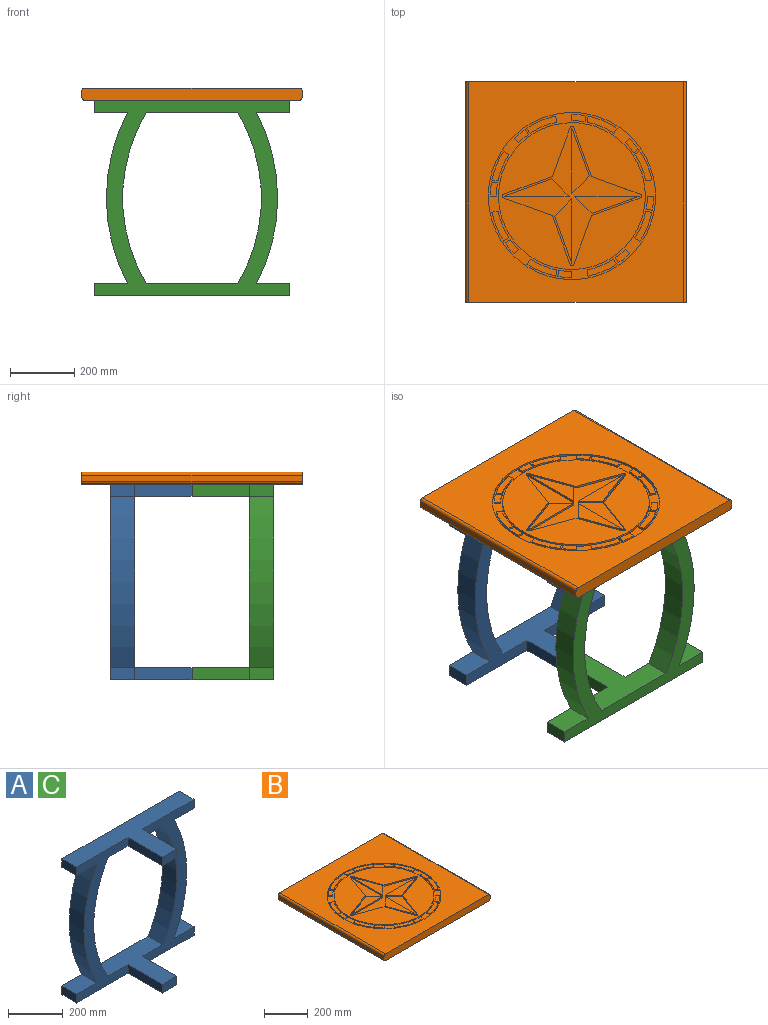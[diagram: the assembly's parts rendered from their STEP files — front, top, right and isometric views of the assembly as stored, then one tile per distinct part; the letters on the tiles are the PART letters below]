
ASSEMBLY  parts=3 mates=2
PART A: 25 faces, bbox 609.6x254x609.6 mm
  f0: plane 609.6x266.7mm, normal (0,-1,0), area 48635.2mm2, adj f2,f3,f4,f5,f6,f7,f8,f13
  f1: plane 609.6x266.7mm, normal (0,-1,0), area 48635.2mm2, adj f2,f8,f9,f10,f11,f12,f14,f15
  f2: plane 609.6x254mm, normal (0,0,1), area 59999.9mm2, adj f0,f1,f3,f17,f18,f22,f23,f24
  f3: plane 76.2x38.1mm, normal (-1,0,0), area 2903.2mm2, adj f0,f2,f4,f18
  f4: plane 104.15x76.2mm, normal (0,0,-1), area 7936mm2, adj f0,f3,f5,f18
  f5: cylinder r=571.5mm len=533.4mm, axis (0,1,0), area 42287mm2, adj f0,f4,f6,f18
  f6: plane 104.15x76.2mm, normal (0,0,1), area 7936mm2, adj f0,f5,f7,f18
  f7: plane 76.2x38.1mm, normal (-1,0,0), area 2903.2mm2, adj f0,f6,f8,f18
  f8: plane 609.6x254mm, normal (0,0,-1), area 59999.9mm2, adj f0,f1,f7,f9,f18,f19,f20,f21
  f9: plane 76.2x38.1mm, normal (1,0,0), area 2903.2mm2, adj f1,f8,f10,f18
  f10: plane 104.15x76.2mm, normal (0,0,1), area 7936mm2, adj f1,f9,f11,f18
  f11: cylinder r=571.5mm len=533.4mm, axis (0,1,0), area 42287mm2, adj f1,f10,f12,f18
  f12: plane 104.15x76.2mm, normal (0,0,-1), area 7936mm2, adj f1,f11,f17,f18
  f13: cylinder r=520.7mm len=533.4mm, axis (0,1,0), area 42672.1mm2, adj f0,f14,f16,f18
  f14: plane 284.83x254mm, normal (0,0,-1), area 35252.1mm2, adj f0,f1,f13,f15,f18,f22,f23,f24
  f15: cylinder r=520.7mm len=533.4mm, axis (0,1,0), area 42672.1mm2, adj f1,f14,f16,f18
  f16: plane 284.83x254mm, normal (0,0,1), area 35252.1mm2, adj f0,f1,f13,f15,f18,f19,f20,f21
  f17: plane 76.2x38.1mm, normal (1,0,0), area 2903.2mm2, adj f1,f2,f12,f18
  f18: plane 609.6x609.6mm, normal (0,1,0), area 103076.8mm2, adj f2,f3,f4,f5,f6,f7,f8,f9
  f19: plane 177.8x38.1mm, normal (-1,0,0), area 6774.2mm2, adj f0,f8,f16,f21
  f20: plane 177.8x38.1mm, normal (1,0,0), area 6774.2mm2, adj f1,f8,f16,f21
  f21: plane 76.2x38.1mm, normal (0,-1,0), area 2903.2mm2, adj f8,f16,f19,f20
  f22: plane 177.8x38.1mm, normal (-1,0,0), area 6774.2mm2, adj f0,f2,f14,f24
  f23: plane 177.8x38.1mm, normal (1,0,0), area 6774.2mm2, adj f1,f2,f14,f24
  f24: plane 76.2x38.1mm, normal (0,-1,0), area 2903.2mm2, adj f2,f14,f22,f23
PART B: 123 faces, bbox 685.8x685.8x38.1 mm
  f0: plane 457.2x457.2mm, normal (0,0,1), area 108640mm2, adj f76,f96,f97,f98,f99,f100,f101,f102
  f1: plane 685.8x666.75mm, normal (0,0,1), area 244313.3mm2, adj f3,f5,f9,f10,f59
  f2: plane 685.8x19.05mm, normal (-1,0,0), area 13064.5mm2, adj f3,f5,f8,f10
  f3: plane 685.8x38.1mm, normal (0,-1,0), area 26051.1mm2, adj f1,f2,f4,f6,f7,f8,f9,f10
  f4: plane 685.8x19.05mm, normal (1,0,0), area 13064.5mm2, adj f3,f5,f7,f9
  f5: plane 685.8x38.1mm, normal (0,1,0), area 26051.1mm2, adj f1,f2,f4,f6,f7,f8,f9,f10
  f6: plane 685.8x666.75mm, normal (0,0,-1), area 457257.1mm2, adj f3,f5,f7,f8
  f7: cylinder r=9.53mm len=685.8mm, axis (0,1,0), area 10260.8mm2, adj f3,f4,f5,f6
  f8: cylinder r=9.53mm len=685.8mm, axis (0,-1,0), area 10260.8mm2, adj f2,f3,f5,f6
  f9: cylinder r=9.53mm len=685.8mm, axis (0,-1,0), area 10260.8mm2, adj f1,f3,f4,f5
  f10: cylinder r=9.53mm len=685.8mm, axis (0,1,0), area 10260.8mm2, adj f1,f2,f3,f5
  f11: cylinder r=254mm len=90.1mm, axis (0,0,1), area 623.1mm2, adj f12,f60,f77,f93
  f12: plane 18.77x6.35mm, normal (0.17,-0.98,0), area 121mm2, adj f11,f13,f77,f93
  f13: cylinder r=234.95mm len=82.47mm, axis (0,0,1), area 570.3mm2, adj f12,f60,f77,f93
  f14: cylinder r=254mm len=33.92mm, axis (0,0,1), area 281.5mm2, adj f15,f61,f77,f92
  f15: plane 15.61x10.93mm, normal (0.57,-0.82,0), area 121mm2, adj f14,f16,f77,f92
  f16: cylinder r=234.95mm len=31.37mm, axis (0,0,1), area 260.4mm2, adj f15,f61,f77,f92
  f17: cylinder r=254mm len=33.92mm, axis (0,0,1), area 281.5mm2, adj f18,f62,f77,f91
  f18: plane 15.61x10.93mm, normal (0.82,0.57,0), area 121mm2, adj f17,f19,f77,f91
  f19: cylinder r=234.95mm len=31.37mm, axis (0,0,1), area 260.4mm2, adj f18,f62,f77,f91
  f20: cylinder r=254mm len=90.1mm, axis (0,0,1), area 623.1mm2, adj f21,f63,f77,f90
  f21: plane 15.61x10.93mm, normal (0.57,0.82,0), area 121mm2, adj f20,f22,f77,f90
  f22: cylinder r=234.95mm len=82.47mm, axis (0,0,1), area 570.3mm2, adj f21,f63,f77,f90
  f23: cylinder r=254mm len=44.11mm, axis (0,0,1), area 281.5mm2, adj f24,f64,f77,f89
  f24: plane 18.76x6.35mm, normal (0.17,0.98,0), area 121mm2, adj f23,f25,f77,f89
  f25: cylinder r=234.95mm len=40.8mm, axis (0,0,1), area 260.4mm2, adj f24,f64,f77,f89
  f26: cylinder r=254mm len=90.1mm, axis (0,0,1), area 623.1mm2, adj f27,f65,f77,f88
  f27: plane 18.77x6.35mm, normal (-0.17,0.98,0), area 121mm2, adj f26,f28,f77,f88
  f28: cylinder r=234.95mm len=82.47mm, axis (0,0,1), area 570.3mm2, adj f27,f65,f77,f88
  f29: cylinder r=254mm len=33.92mm, axis (0,0,1), area 281.5mm2, adj f30,f66,f77,f87
  f30: plane 15.61x10.93mm, normal (-0.57,0.82,0), area 121mm2, adj f29,f31,f77,f87
  f31: cylinder r=234.95mm len=31.37mm, axis (0,0,1), area 260.4mm2, adj f30,f66,f77,f87
  f32: cylinder r=254mm len=90.1mm, axis (0,0,1), area 623.1mm2, adj f33,f67,f77,f86
  f33: plane 15.61x10.93mm, normal (-0.82,0.57,0), area 121mm2, adj f32,f34,f77,f86
  f34: cylinder r=234.95mm len=82.47mm, axis (0,0,1), area 570.3mm2, adj f33,f67,f77,f86
  f35: cylinder r=254mm len=44.11mm, axis (0,0,1), area 281.5mm2, adj f36,f68,f77,f85
  f36: plane 18.76x6.35mm, normal (-0.98,0.17,0), area 121mm2, adj f35,f37,f77,f85
  f37: cylinder r=234.95mm len=40.8mm, axis (0,0,1), area 260.4mm2, adj f36,f68,f77,f85
  f38: cylinder r=254mm len=90.1mm, axis (0,0,1), area 623.1mm2, adj f39,f69,f77,f84
  f39: plane 18.77x6.35mm, normal (-0.98,-0.17,0), area 121mm2, adj f38,f40,f77,f84
  f40: cylinder r=234.95mm len=82.47mm, axis (0,0,1), area 570.3mm2, adj f39,f69,f77,f84
  f41: cylinder r=254mm len=33.92mm, axis (0,0,1), area 281.5mm2, adj f42,f70,f77,f83
  f42: plane 15.61x10.93mm, normal (-0.82,-0.57,0), area 121mm2, adj f41,f43,f77,f83
  f43: cylinder r=234.95mm len=31.37mm, axis (0,0,1), area 260.4mm2, adj f42,f70,f77,f83
  f44: cylinder r=254mm len=90.1mm, axis (0,0,1), area 623.1mm2, adj f45,f71,f77,f82
  f45: plane 15.61x10.93mm, normal (-0.57,-0.82,0), area 121mm2, adj f44,f46,f77,f82
  f46: cylinder r=234.95mm len=82.47mm, axis (0,0,1), area 570.3mm2, adj f45,f71,f77,f82
  f47: cylinder r=254mm len=44.11mm, axis (0,0,1), area 281.5mm2, adj f48,f72,f77,f81
  f48: plane 18.76x6.35mm, normal (-0.17,-0.98,0), area 121mm2, adj f47,f49,f77,f81
  f49: cylinder r=234.95mm len=40.8mm, axis (0,0,1), area 260.4mm2, adj f48,f72,f77,f81
  f50: cylinder r=234.95mm len=82.47mm, axis (0,0,1), area 570.3mm2, adj f51,f73,f77,f80
  f51: plane 18.77x6.35mm, normal (-0.98,0.17,0), area 121mm2, adj f50,f52,f77,f80
  f52: cylinder r=254mm len=90.1mm, axis (0,0,1), area 623.1mm2, adj f51,f73,f77,f80
  f53: plane 18.77x6.35mm, normal (0.98,0.17,0), area 121mm2, adj f54,f74,f77,f79
  f54: cylinder r=234.95mm len=82.47mm, axis (0,0,1), area 570.3mm2, adj f53,f55,f77,f79
  f55: plane 15.61x10.93mm, normal (-0.82,-0.57,0), area 121mm2, adj f54,f74,f77,f79
  f56: cylinder r=234.95mm len=40.8mm, axis (0,0,1), area 260.4mm2, adj f57,f75,f77,f78
  f57: plane 19.05x6.35mm, normal (-1,0,0), area 121mm2, adj f56,f58,f77,f78
  f58: cylinder r=254mm len=44.11mm, axis (0,0,1), area 281.5mm2, adj f57,f75,f77,f78
  f59: cylinder r=260.35mm len=520.7mm, axis (0,0,1), area 10387.5mm2, adj f1,f77
  f60: plane 15.61x10.93mm, normal (-0.57,0.82,0), area 121mm2, adj f11,f13,f77,f93
  f61: plane 13.47x13.47mm, normal (-0.71,0.71,0), area 121mm2, adj f14,f16,f77,f92
  f62: plane 13.47x13.47mm, normal (-0.71,-0.71,0), area 121mm2, adj f17,f19,f77,f91
  f63: plane 18.77x6.35mm, normal (-0.17,-0.98,0), area 121mm2, adj f20,f22,f77,f90
  f64: plane 19.05x6.35mm, normal (0,-1,0), area 121mm2, adj f23,f25,f77,f89
  f65: plane 15.61x10.93mm, normal (0.57,-0.82,0), area 121mm2, adj f26,f28,f77,f88
  f66: plane 13.47x13.47mm, normal (0.71,-0.71,0), area 121mm2, adj f29,f31,f77,f87
  f67: plane 18.77x6.35mm, normal (0.98,-0.17,0), area 121mm2, adj f32,f34,f77,f86
  f68: plane 19.05x6.35mm, normal (1,0,0), area 121mm2, adj f35,f37,f77,f85
  f69: plane 15.61x10.93mm, normal (0.82,0.57,0), area 121mm2, adj f38,f40,f77,f84
  f70: plane 13.47x13.47mm, normal (0.71,0.71,0), area 121mm2, adj f41,f43,f77,f83
  f71: plane 18.77x6.35mm, normal (0.17,0.98,0), area 121mm2, adj f44,f46,f77,f82
  f72: plane 19.05x6.35mm, normal (0,1,0), area 121mm2, adj f47,f49,f77,f81
  f73: plane 15.61x10.93mm, normal (0.82,-0.57,0), area 121mm2, adj f50,f52,f77,f80
  f74: cylinder r=254mm len=90.1mm, axis (0,0,1), area 623.1mm2, adj f53,f55,f77,f79
  f75: plane 18.76x6.35mm, normal (0.98,-0.17,0), area 121mm2, adj f56,f58,f77,f78
  f76: cylinder r=228.6mm len=457.2mm, axis (0,0,1), area 9120.7mm2, adj f0,f77
  f77: plane 520.7x520.7mm, normal (0,0,1), area 27946.7mm2, adj f11,f12,f13,f14,f15,f16,f17,f18
  f78: plane 44.11x22.62mm, normal (0,0,1), area 812.8mm2, adj f56,f57,f58,f75
  f79: plane 93.4x52.93mm, normal (0,0,1), area 1790.1mm2, adj f53,f54,f55,f74
  f80: plane 93.4x52.93mm, normal (0,0,1), area 1790.1mm2, adj f50,f51,f52,f73
  f81: plane 44.11x22.62mm, normal (0,0,1), area 812.8mm2, adj f47,f48,f49,f72
  f82: plane 93.4x52.93mm, normal (0,0,1), area 1790.1mm2, adj f44,f45,f46,f71
  f83: plane 44.84x41.93mm, normal (0,0,1), area 812.8mm2, adj f41,f42,f43,f70
  f84: plane 93.4x52.93mm, normal (0,0,1), area 1790.1mm2, adj f38,f39,f40,f69
  f85: plane 44.11x22.62mm, normal (0,0,1), area 812.8mm2, adj f35,f36,f37,f68
  f86: plane 93.4x52.93mm, normal (0,0,1), area 1790.1mm2, adj f32,f33,f34,f67
  f87: plane 44.84x41.93mm, normal (0,0,1), area 812.8mm2, adj f29,f30,f31,f66
  f88: plane 93.4x52.93mm, normal (0,0,1), area 1790.1mm2, adj f26,f27,f28,f65
  f89: plane 44.11x22.62mm, normal (0,0,1), area 812.8mm2, adj f23,f24,f25,f64
  f90: plane 93.4x52.93mm, normal (0,0,1), area 1790.1mm2, adj f20,f21,f22,f63
  f91: plane 44.84x41.93mm, normal (0,0,1), area 812.8mm2, adj f17,f18,f19,f62
  f92: plane 44.84x41.93mm, normal (0,0,1), area 812.8mm2, adj f14,f15,f16,f61
  f93: plane 93.4x52.93mm, normal (0,0,1), area 1790.1mm2, adj f11,f12,f13,f60
  f94: plane 147.4x53.65mm, normal (-0.34,0.94,0), area 996.1mm2, adj f95,f114,f115,f116
  f95: plane 53.65x53.65mm, normal (0.71,0.71,0), area 481.8mm2, adj f94,f114,f115,f116
  f96: plane 151.2x55.03mm, normal (-0.34,0.94,0), area 1021.8mm2, adj f0,f97,f112,f116
  f97: cylinder r=6.35mm len=11.93mm, axis (0,0,1), area 98.5mm2, adj f0,f96,f98,f116
  f98: plane 151.2x55.03mm, normal (-0.34,-0.94,0), area 1021.8mm2, adj f0,f97,f99,f116
  f99: plane 151.2x55.03mm, normal (-0.94,-0.34,0), area 1021.8mm2, adj f0,f98,f100,f116
  f100: cylinder r=6.35mm len=11.93mm, axis (0,0,1), area 98.5mm2, adj f0,f99,f101,f116
  f101: plane 151.2x55.03mm, normal (0.94,-0.34,0), area 1021.8mm2, adj f0,f100,f102,f116
  f102: plane 151.2x55.03mm, normal (0.34,-0.94,0), area 1021.8mm2, adj f0,f101,f103,f116
  f103: cylinder r=6.35mm len=11.93mm, axis (0,0,1), area 98.5mm2, adj f0,f102,f104,f116
  f104: plane 151.2x55.03mm, normal (0.34,0.94,0), area 1021.8mm2, adj f0,f103,f105,f116
  f105: plane 151.2x55.03mm, normal (0.94,0.34,0), area 1021.8mm2, adj f0,f104,f106,f116
  f106: cylinder r=6.35mm len=11.93mm, axis (0,0,1), area 98.5mm2, adj f0,f105,f112,f116
  f107: plane 147.4x53.65mm, normal (-0.94,-0.34,0), area 996.1mm2, adj f108,f116,f117,f118
  f108: plane 53.65x53.65mm, normal (-0.71,0.71,0), area 481.8mm2, adj f107,f116,f117,f118
  f109: plane 147.4x53.65mm, normal (0.34,-0.94,0), area 996.1mm2, adj f113,f116,f119,f120
  f110: plane 147.4x53.65mm, normal (0.94,0.34,0), area 996.1mm2, adj f111,f116,f121,f122
  f111: plane 53.65x53.65mm, normal (0.71,-0.71,0), area 481.8mm2, adj f110,f116,f121,f122
  f112: plane 151.2x55.03mm, normal (-0.94,0.34,0), area 1021.8mm2, adj f0,f96,f106,f116
  f113: plane 53.65x53.65mm, normal (-0.71,-0.71,0), area 481.8mm2, adj f109,f116,f119,f120
  f114: plane 201.05x53.65mm, normal (0,0,1), area 5393.3mm2, adj f94,f95,f115
  f115: plane 201.05x6.35mm, normal (0,-1,0), area 1276.7mm2, adj f94,f95,f114,f116
  f116: plane 432.77x432.77mm, normal (0,0,1), area 33960.1mm2, adj f94,f95,f96,f97,f98,f99,f100,f101
  f117: plane 201.05x53.65mm, normal (0,0,1), area 5393.3mm2, adj f107,f108,f118
  f118: plane 201.05x6.35mm, normal (1,0,0), area 1276.7mm2, adj f107,f108,f116,f117
  f119: plane 201.05x53.65mm, normal (0,0,1), area 5393.3mm2, adj f109,f113,f120
  f120: plane 201.05x6.35mm, normal (0,1,0), area 1276.7mm2, adj f109,f113,f116,f119
  f121: plane 201.05x53.65mm, normal (0,0,1), area 5393.3mm2, adj f110,f111,f122
  f122: plane 201.05x6.35mm, normal (-1,0,0), area 1276.7mm2, adj f110,f111,f116,f121
PART C: same geometry as A
PLACE A t=(-694.78,126.5,-140.54)mm
PLACE B t=(-402.68,-140.2,469.06)mm
PLACE C rot(axis=(0,0,1),180deg) t=(-85.18,-381.5,-140.54)mm
MATE fastened A.f8 <-> C.f8  axis (0,0,-1) through (-389.98,-127.5,-140.54)mm
MATE fastened B.f6 <-> C.f2  axis (0,0,-1) through (-389.98,-127.5,469.06)mm
